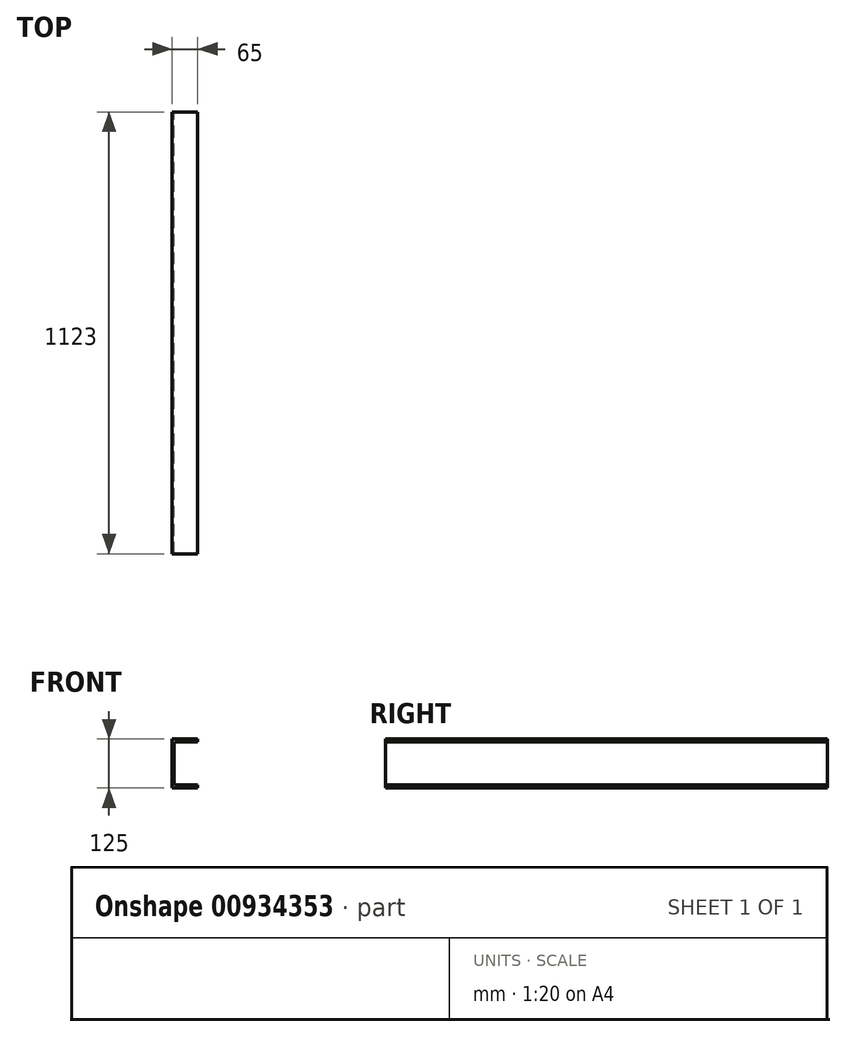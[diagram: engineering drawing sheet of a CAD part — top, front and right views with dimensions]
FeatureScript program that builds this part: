
annotation { "Feature Type Name" : "Feature", "Feature Type Description" : "" }
export const myFeature = defineFeature(function(context is Context, id is Id, definition is map)
    precondition{}
    {
        {
            var Q0;
            Q0=qCreatedBy(makeId("Front.planeOp"),FACE);
            var sketch = newSketch(context, id + "F0", { "sketchPlane" : qUnion([Q0])});
            skLineSegment(sketch, "E0", {"start": v(-25.17, -62.5) * mm, "end": v(-25.17, 62.5) * mm});
            skLineSegment(sketch, "E1", {"start": v(-25.17, 62.5) * mm, "end": v(39.83, 62.5) * mm});
            skLineSegment(sketch, "E2", {"start": v(39.83, 62.5) * mm, "end": v(39.83, 55) * mm});
            skLineSegment(sketch, "E3", {"start": v(39.83, 55) * mm, "end": v(-12.47, 55) * mm});
            skLineSegment(sketch, "E4", {"start": v(-25.17, -62.5) * mm, "end": v(39.83, -62.5) * mm});
            skLineSegment(sketch, "E5", {"start": v(39.83, -62.5) * mm, "end": v(39.83, -55) * mm});
            skLineSegment(sketch, "E6", {"start": v(39.83, -55) * mm, "end": v(-12.47, -55) * mm});
            skLineSegment(sketch, "E7", {"start": v(-20.47, -47) * mm, "end": v(-20.47, 47) * mm});
            skPoint(sketch, "E8.visualSharp", {"position": v(-20.47, 55) * mm});
            skArc(sketch, "E8.filletArc", {"start": v(-12.47, 55) * mm, "mid": v(-18.12, 52.66) * mm, "end": v(-20.47, 47) * mm});
            skPoint(sketch, "E9.visualSharp", {"position": v(-20.47, -55) * mm});
            skArc(sketch, "E9.filletArc", {"start": v(-20.47, -47) * mm, "mid": v(-18.12, -52.66) * mm, "end": v(-12.47, -55) * mm});
            skSolve(sketch);
        }
        {
            var Q0;
            Q0=makeQuery(id+"F0.imprint","IMPRINT",FACE,{"disambiguationData":[TD([[makeQuery(id+"F0.imprint","IMPRINT",EDGE,{"derivedFrom":sQuery(id+"F0.wireOp",EDGE,"E0")}),-1.0]])]});
            extrude(context, id + "F1", {"entities" : qUnion([Q0]), "depth" : 1123 * mm, "offsetDistance" : 25 * mm});
        }
    });
